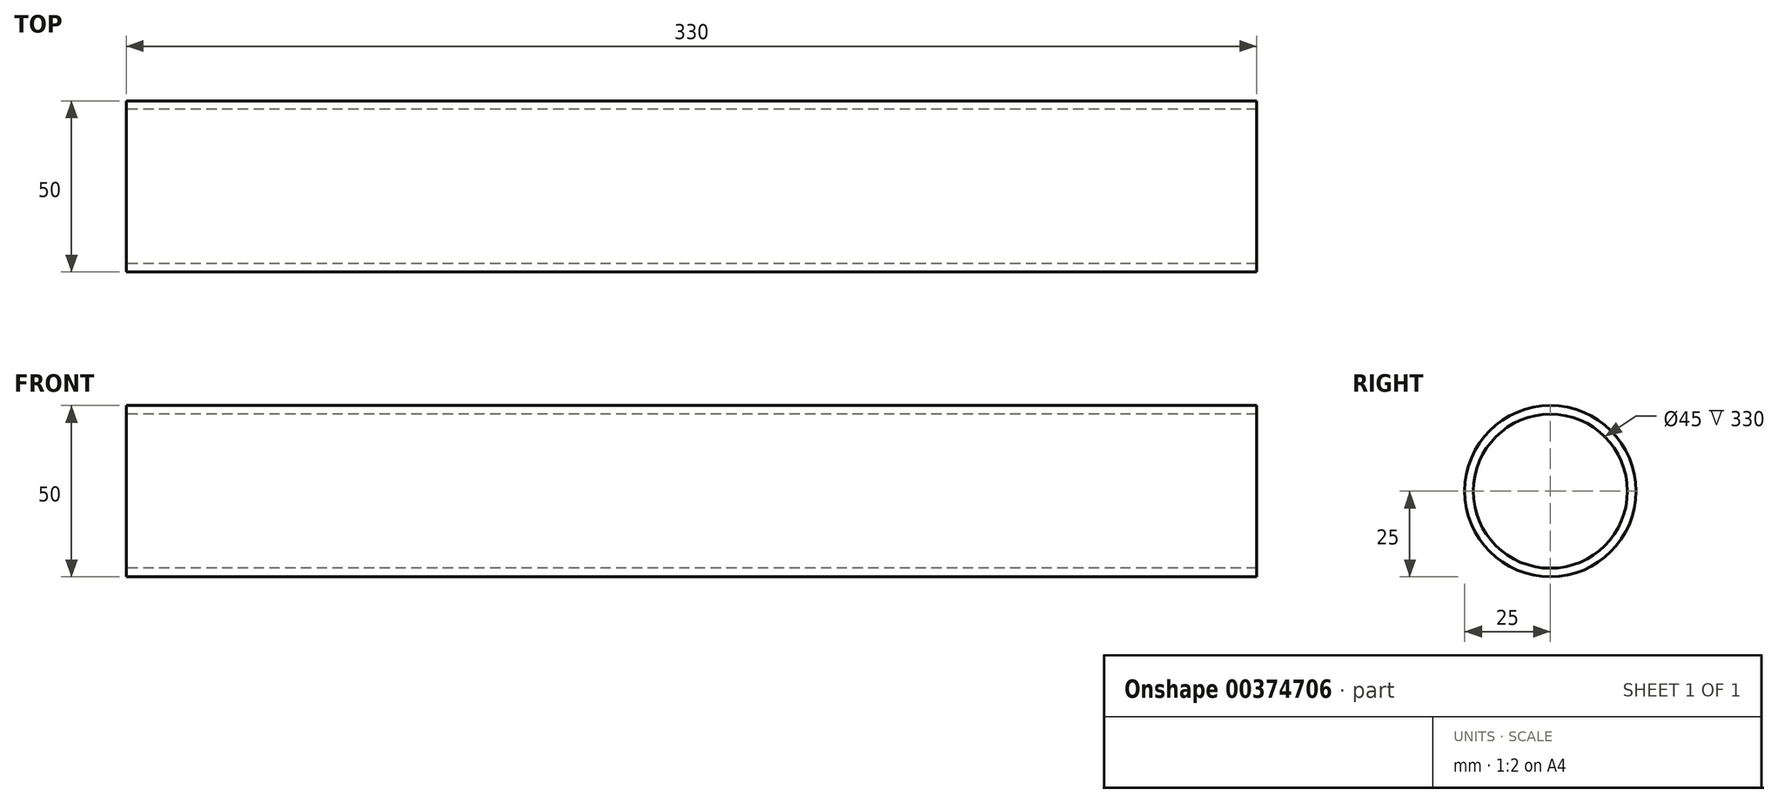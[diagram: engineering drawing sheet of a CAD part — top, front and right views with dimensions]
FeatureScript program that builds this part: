
annotation { "Feature Type Name" : "Feature", "Feature Type Description" : "" }
export const myFeature = defineFeature(function(context is Context, id is Id, definition is map)
    precondition{}
    {
        {
            var Q0;
            Q0=qCreatedBy(makeId("Right.planeOp"),FACE);
            var sketch = newSketch(context, id + "F0", { "sketchPlane" : qUnion([Q0])});
            skCircle(sketch, "E0", {"center": v(0, 0) * mm, "radius": 22.5 * mm});
            skCircle(sketch, "E1", {"center": v(0, 0) * mm, "radius": 25 * mm});
            skSolve(sketch);
        }
        {
            var Q0;
            Q0=makeQuery(id+"F0.imprint","IMPRINT",FACE,{"disambiguationData":[TD([[makeQuery(id+"F0.imprint","IMPRINT",EDGE,{"derivedFrom":sQuery(id+"F0.wireOp",EDGE,"E0")}),-1.0]])]});
            extrude(context, id + "F1", {"entities" : qUnion([Q0]), "endBound" : BoundingType.SYMMETRIC, "depth" : 330 * mm});
        }
    });
